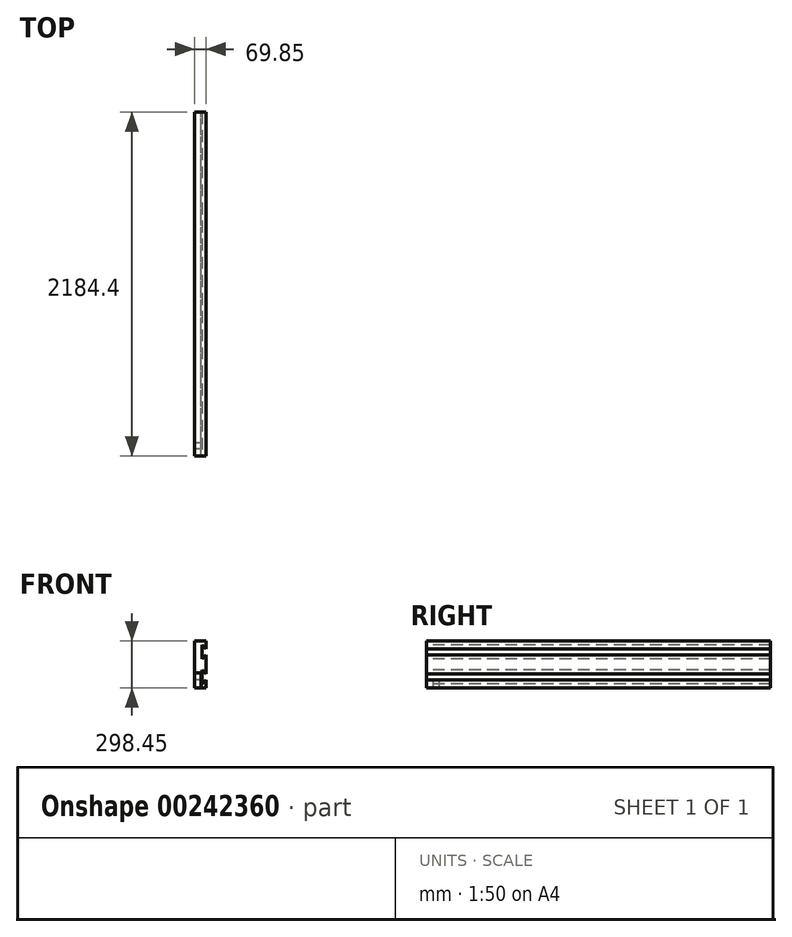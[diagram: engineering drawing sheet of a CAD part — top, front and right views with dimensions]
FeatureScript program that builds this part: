
annotation { "Feature Type Name" : "Feature", "Feature Type Description" : "" }
export const myFeature = defineFeature(function(context is Context, id is Id, definition is map)
    precondition{}
    {
        {
            var Q0;
            Q0=qCreatedBy(makeId("Right.planeOp"),FACE);
            var sketch = newSketch(context, id + "F0", { "sketchPlane" : qUnion([Q0])});
            skLineSegment(sketch, "E0.bottom", {"start": v(0, 0) * mm, "end": v(2184.4, 0) * mm});
            skLineSegment(sketch, "E0.top", {"start": v(0, 95.25) * mm, "end": v(2184.4, 95.25) * mm});
            skLineSegment(sketch, "E0.left", {"start": v(0, 0) * mm, "end": v(0, 95.25) * mm});
            skLineSegment(sketch, "E0.right", {"start": v(2184.4, 0) * mm, "end": v(2184.4, 95.25) * mm});
            skLineSegment(sketch, "E1.bottom", {"start": v(44.45, 0) * mm, "end": v(82.55, 0) * mm});
            skLineSegment(sketch, "E1.top", {"start": v(44.45, 50.8) * mm, "end": v(82.55, 50.8) * mm});
            skLineSegment(sketch, "E1.left", {"start": v(44.45, 0) * mm, "end": v(44.45, 50.8) * mm});
            skLineSegment(sketch, "E1.right", {"start": v(82.55, 0) * mm, "end": v(82.55, 50.8) * mm});
            skLineSegment(sketch, "E2", {"start": v(0, 0) * mm, "end": v(44.45, 0) * mm, "construction": true});
            skSolve(sketch);
        }
        {
            var Q0;
            Q0=makeQuery(id+"F0.imprint","IMPRINT",FACE,{"disambiguationData":[TD([[makeQuery(id+"F0.imprint","IMPRINT",EDGE,{"derivedFrom":sQuery(id+"F0.wireOp",EDGE,"E0.bottom")}),1.0]])]});
            extrude(context, id + "F1", {"entities" : qUnion([Q0]), "depth" : 38.1 * mm});
        }
        {
            var Q0;
            Q0=qCreatedBy(makeId("Front.planeOp"),FACE);
            var sketch = newSketch(context, id + "F2", { "sketchPlane" : qUnion([Q0])});
            skLineSegment(sketch, "E3.bottom", {"start": v(0, 0) * mm, "end": v(69.85, 0) * mm});
            skLineSegment(sketch, "E3.top", {"start": v(0, 298.45) * mm, "end": v(69.85, 298.45) * mm});
            skLineSegment(sketch, "E3.left", {"start": v(0, 0) * mm, "end": v(0, 298.45) * mm});
            skLineSegment(sketch, "E3.right", {"start": v(69.85, 0) * mm, "end": v(69.85, 298.45) * mm});
            skLineSegment(sketch, "E4", {"start": v(69.85, 298.45) * mm, "end": v(69.85, 247.65) * mm, "construction": true});
            skLineSegment(sketch, "E5", {"start": v(44.45, 273.05) * mm, "end": v(44.45, 184.15) * mm});
            skLineSegment(sketch, "E6", {"start": v(69.85, 247.65) * mm, "end": v(44.45, 273.05) * mm});
            skLineSegment(sketch, "E7", {"start": v(69.85, 247.65) * mm, "end": v(69.85, 209.55) * mm, "construction": true});
            skLineSegment(sketch, "E8", {"start": v(69.85, 209.55) * mm, "end": v(44.45, 184.15) * mm});
            skArc(sketch, "E9", {"start": v(44.45, 273.05) * mm, "mid": v(56.1, 280.84) * mm, "end": v(69.85, 283.57) * mm, "construction": true});
            skArc(sketch, "E10", {"start": v(44.45, 184.15) * mm, "mid": v(56.1, 176.36) * mm, "end": v(69.85, 173.63) * mm, "construction": true});
            skLineSegment(sketch, "E11", {"start": v(69.85, 228.6) * mm, "end": v(44.45, 228.6) * mm, "construction": true});
            skLineSegment(sketch, "E12", {"start": v(69.85, 88.9) * mm, "end": v(44.45, 114.3) * mm});
            skLineSegment(sketch, "E13", {"start": v(44.45, 114.3) * mm, "end": v(44.45, 25.4) * mm});
            skLineSegment(sketch, "E14", {"start": v(44.45, 25.4) * mm, "end": v(69.85, 50.8) * mm});
            skArc(sketch, "E15", {"start": v(44.45, 114.3) * mm, "mid": v(56.1, 122.09) * mm, "end": v(69.85, 124.82) * mm, "construction": true});
            skArc(sketch, "E16", {"start": v(44.45, 25.4) * mm, "mid": v(56.1, 17.61) * mm, "end": v(69.85, 14.88) * mm, "construction": true});
            skLineSegment(sketch, "E17", {"start": v(44.45, 69.85) * mm, "end": v(69.85, 69.85) * mm, "construction": true});
            skLineSegment(sketch, "E18", {"start": v(69.85, 88.9) * mm, "end": v(69.85, 50.8) * mm, "construction": true});
            skLineSegment(sketch, "E19", {"start": v(69.85, 0) * mm, "end": v(69.85, 50.8) * mm, "construction": true});
            skSolve(sketch);
        }
        {
            var Q0;
            {var subQ5=sQuery(id+"F2.wireOp",EDGE,"E3.bottom");Q0=makeQuery(id+"F2.imprint","IMPRINT",FACE,{"disambiguationData":[TD([[makeQuery(id+"F2.imprint","IMPRINT",EDGE,{"derivedFrom":subQ5}),1.0]])]});}
            extrude(context, id + "F3", {"entities" : qUnion([Q0]), "oppositeDirection" : true, "depth" : 2184.4 * mm});
        }
    });
